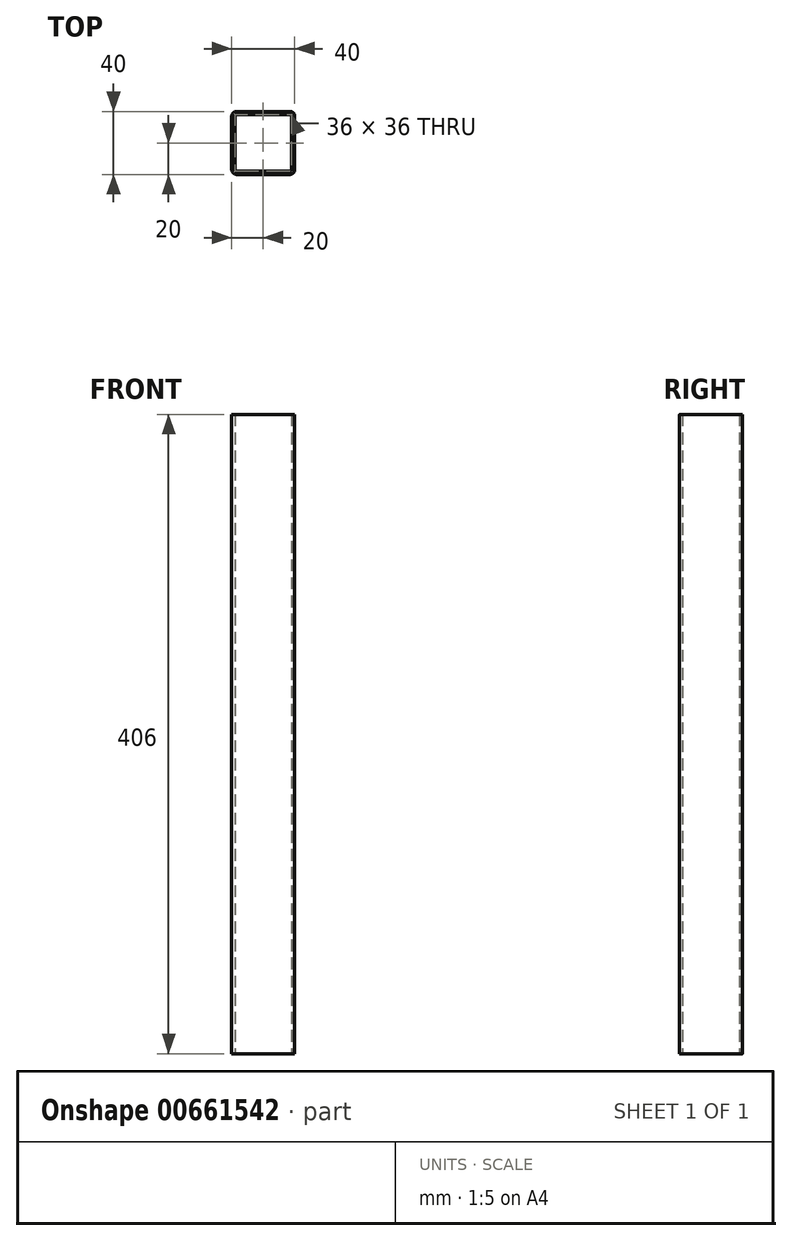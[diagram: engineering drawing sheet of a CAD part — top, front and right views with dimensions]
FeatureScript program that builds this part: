
annotation { "Feature Type Name" : "Feature", "Feature Type Description" : "" }
export const myFeature = defineFeature(function(context is Context, id is Id, definition is map)
    precondition{}
    {
        {
            var Q0;
            Q0=qCreatedBy(makeId("Top.planeOp"),FACE);
            var sketch = newSketch(context, id + "F0", { "sketchPlane" : qUnion([Q0])});
            skLineSegment(sketch, "E0.bottom", {"start": v(-17, 20) * mm, "end": v(17, 20) * mm});
            skLineSegment(sketch, "E0.top", {"start": v(-17, -20) * mm, "end": v(17, -20) * mm});
            skLineSegment(sketch, "E0.left", {"start": v(-20, 17) * mm, "end": v(-20, -17) * mm});
            skLineSegment(sketch, "E0.right", {"start": v(20, 17) * mm, "end": v(20, -17) * mm});
            skPoint(sketch, "E0.middle", {"position": v(0, 0) * mm});
            skPoint(sketch, "E1.visualSharp", {"position": v(-20, 20) * mm});
            skArc(sketch, "E1.filletArc", {"start": v(-17, 20) * mm, "mid": v(-19.12, 19.12) * mm, "end": v(-20, 17) * mm});
            skPoint(sketch, "E2.visualSharp", {"position": v(20, 20) * mm});
            skArc(sketch, "E2.filletArc", {"start": v(20, 17) * mm, "mid": v(19.12, 19.12) * mm, "end": v(17, 20) * mm});
            skPoint(sketch, "E3.visualSharp", {"position": v(20, -20) * mm});
            skArc(sketch, "E3.filletArc", {"start": v(17, -20) * mm, "mid": v(19.12, -19.12) * mm, "end": v(20, -17) * mm});
            skPoint(sketch, "E4.visualSharp", {"position": v(-20, -20) * mm});
            skArc(sketch, "E4.filletArc", {"start": v(-20, -17) * mm, "mid": v(-19.12, -19.12) * mm, "end": v(-17, -20) * mm});
            skLineSegment(sketch, "E5.0", {"start": v(-18, 18) * mm, "end": v(-18, -18) * mm});
            skLineSegment(sketch, "E5.1", {"start": v(-18, 18) * mm, "end": v(18, 18) * mm});
            skLineSegment(sketch, "E5.2", {"start": v(18, 18) * mm, "end": v(18, -18) * mm});
            skLineSegment(sketch, "E5.3", {"start": v(-18, -18) * mm, "end": v(18, -18) * mm});
            skSolve(sketch);
        }
        {
            var Q0;
            Q0=makeQuery(id+"F0.imprint","IMPRINT",FACE,{"disambiguationData":[TD([[makeQuery(id+"F0.imprint","IMPRINT",EDGE,{"derivedFrom":sQuery(id+"F0.wireOp",EDGE,"E0.bottom")}),-1.0]])]});
            extrude(context, id + "F1", {"entities" : qUnion([Q0]), "depth" : 406 * mm, "offsetDistance" : 25 * mm});
        }
    });
